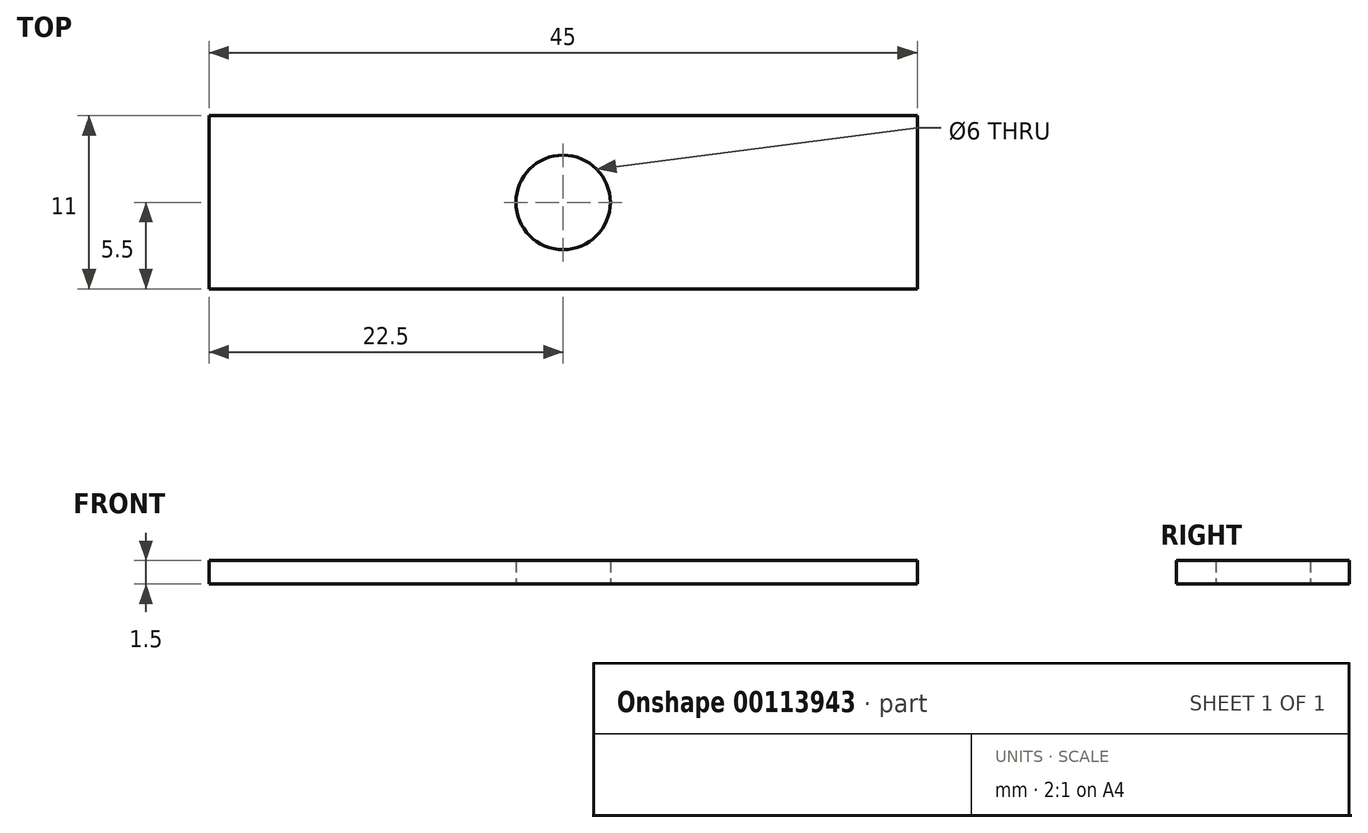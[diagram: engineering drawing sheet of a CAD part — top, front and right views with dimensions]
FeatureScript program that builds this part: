
annotation { "Feature Type Name" : "Feature", "Feature Type Description" : "" }
export const myFeature = defineFeature(function(context is Context, id is Id, definition is map)
    precondition{}
    {
        {
            var Q0;
            Q0=qCreatedBy(makeId("Top.planeOp"),FACE);
            var sketch = newSketch(context, id + "F0", { "sketchPlane" : qUnion([Q0])});
            skLineSegment(sketch, "E0.bottom", {"start": v(22.5, -5.5) * mm, "end": v(-22.5, -5.5) * mm});
            skLineSegment(sketch, "E0.top", {"start": v(22.5, 5.5) * mm, "end": v(-22.5, 5.5) * mm});
            skLineSegment(sketch, "E0.left", {"start": v(22.5, -5.5) * mm, "end": v(22.5, 5.5) * mm});
            skLineSegment(sketch, "E0.right", {"start": v(-22.5, -5.5) * mm, "end": v(-22.5, 5.5) * mm});
            skPoint(sketch, "E0.middle", {"position": v(0, 0) * mm});
            skCircle(sketch, "E1", {"center": v(0, 0) * mm, "radius": 3 * mm});
            skSolve(sketch);
        }
        {
            var Q0;
            Q0=makeQuery(id+"F0.imprint","IMPRINT",FACE,{"disambiguationData":[TD([[makeQuery(id+"F0.imprint","IMPRINT",EDGE,{"derivedFrom":sQuery(id+"F0.wireOp",EDGE,"E0.bottom")}),-1.0]])]});
            extrude(context, id + "F1", {"entities" : qUnion([Q0]), "depth" : 1.5 * mm});
        }
    });
